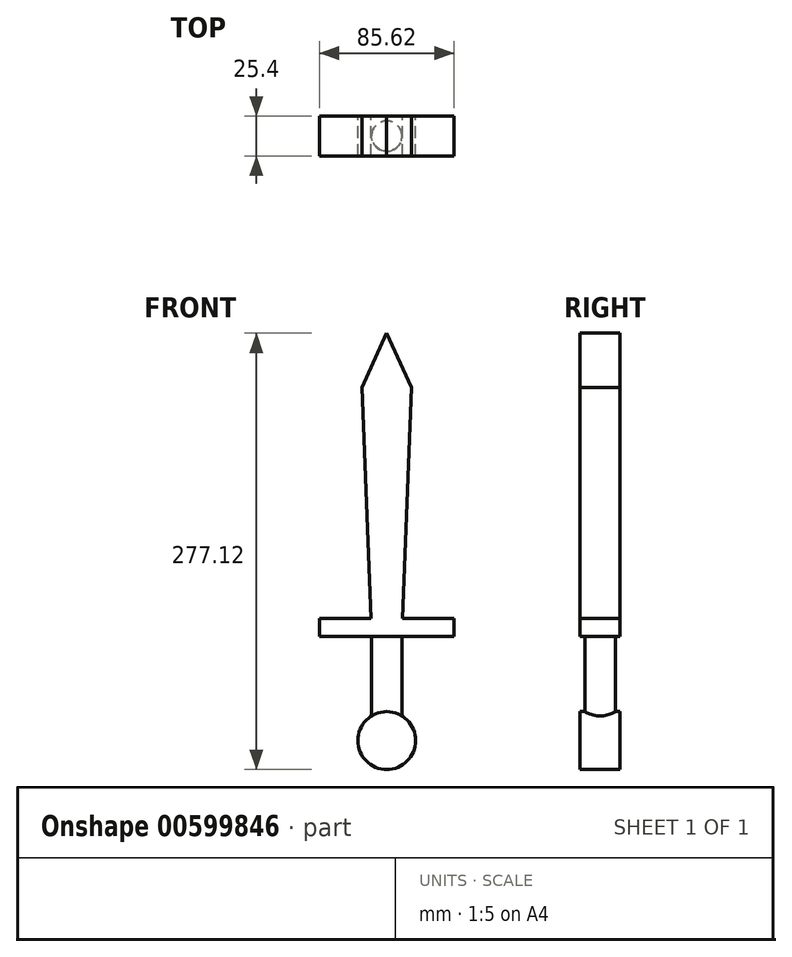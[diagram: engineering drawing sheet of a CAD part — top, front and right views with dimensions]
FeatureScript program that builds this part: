
annotation { "Feature Type Name" : "Feature", "Feature Type Description" : "" }
export const myFeature = defineFeature(function(context is Context, id is Id, definition is map)
    precondition{}
    {
        {
            var Q0;
            Q0=qCreatedBy(makeId("Front.planeOp"),FACE);
            var sketch = newSketch(context, id + "F0", { "sketchPlane" : qUnion([Q0])});
            skCircle(sketch, "E0", {"center": v(0, -49.9) * mm, "radius": 18.37 * mm});
            skLineSegment(sketch, "E1", {"start": v(0, -49.9) * mm, "end": v(0, 22) * mm});
            skLineSegment(sketch, "E2.bottom", {"start": v(0, 22) * mm, "end": v(9.7, 22) * mm});
            skLineSegment(sketch, "E2.top", {"start": v(0, -51.8) * mm, "end": v(9.7, -51.8) * mm});
            skLineSegment(sketch, "E2.left", {"start": v(0, 22) * mm, "end": v(0, -51.8) * mm});
            skLineSegment(sketch, "E2.right", {"start": v(9.7, 22) * mm, "end": v(9.7, -51.8) * mm});
            skLineSegment(sketch, "E3.bottom", {"start": v(0, -51.8) * mm, "end": v(-9.7, -51.8) * mm});
            skLineSegment(sketch, "E3.top", {"start": v(0, 22) * mm, "end": v(-9.7, 22) * mm});
            skLineSegment(sketch, "E3.left", {"start": v(0, -51.8) * mm, "end": v(0, 22) * mm});
            skLineSegment(sketch, "E3.right", {"start": v(-9.7, -51.8) * mm, "end": v(-9.7, 22) * mm});
            skLineSegment(sketch, "E4.bottom", {"start": v(42.81, 27.67) * mm, "end": v(-42.81, 27.67) * mm});
            skLineSegment(sketch, "E4.top", {"start": v(42.81, 16.32) * mm, "end": v(-42.81, 16.32) * mm});
            skLineSegment(sketch, "E4.left", {"start": v(42.81, 27.67) * mm, "end": v(42.81, 16.32) * mm});
            skLineSegment(sketch, "E4.right", {"start": v(-42.81, 27.67) * mm, "end": v(-42.81, 16.32) * mm});
            skPoint(sketch, "E4.middle", {"position": v(0, 22) * mm});
            skLineSegment(sketch, "E5", {"start": v(-9.7, 22) * mm, "end": v(-15.85, 174.32) * mm});
            skLineSegment(sketch, "E6", {"start": v(-15.85, 174.32) * mm, "end": v(0, 208.85) * mm});
            skLineSegment(sketch, "E7.MirrorCS", {"start": v(15.85, 174.32) * mm, "end": v(0, 208.85) * mm});
            skLineSegment(sketch, "E8.MirrorCS", {"start": v(9.7, 22) * mm, "end": v(15.85, 174.32) * mm});
            skSolve(sketch);
        }
        {
            var Q0;
            {var subQ6=sQuery(id+"F0.wireOp",EDGE,"E6");Q0=makeQuery(id+"F0.imprint","IMPRINT",FACE,{"disambiguationData":[TD([[makeQuery(id+"F0.imprint","IMPRINT",EDGE,{"derivedFrom":subQ6}),-1.0]])]});}
            var Q1;
            {var subQ0=sQuery(id+"F0.wireOp",EDGE,"E4.left");Q1=makeQuery(id+"F0.imprint","IMPRINT",FACE,{"disambiguationData":[TD([[makeQuery(id+"F0.imprint","IMPRINT",EDGE,{"derivedFrom":subQ0}),-1.0]])]});}
            var Q2;
            {var subQ0=sQuery(id+"F0.wireOp",EDGE,"E4.right");Q2=makeQuery(id+"F0.imprint","IMPRINT",FACE,{"disambiguationData":[TD([[makeQuery(id+"F0.imprint","IMPRINT",EDGE,{"derivedFrom":subQ0}),1.0]])]});}
            var Q3;
            {var subQ6=sQuery(id+"F0.wireOp",EDGE,"E2.bottom");Q3=makeQuery(id+"F0.imprint","IMPRINT",FACE,{"disambiguationData":[TD([[makeQuery(id+"F0.imprint","IMPRINT",EDGE,{"derivedFrom":subQ6}),1.0]])]});}
            var Q4;
            {var subQ0=sQuery(id+"F0.wireOp",EDGE,"E2.bottom");Q4=makeQuery(id+"F0.imprint","IMPRINT",FACE,{"disambiguationData":[TD([[makeQuery(id+"F0.imprint","IMPRINT",EDGE,{"derivedFrom":subQ0}),-1.0]])]});}
            var Q5;
            {var subQ0=sQuery(id+"F0.wireOp",EDGE,"E3.top");Q5=makeQuery(id+"F0.imprint","IMPRINT",FACE,{"disambiguationData":[TD([[makeQuery(id+"F0.imprint","IMPRINT",EDGE,{"derivedFrom":subQ0}),1.0]])]});}
            extrude(context, id + "F1", {"entities" : qUnion([Q0, Q1, Q2, Q3, Q4, Q5]), "endBound" : BoundingType.SYMMETRIC, "depth" : 25.4 * mm, "offsetDistance" : 25.4 * mm});
        }
        {
            var Q0;
            {var subQ0=sQuery(id+"F0.wireOp",EDGE,"E2.right");var subQ1=sQuery(id+"F0.wireOp",EDGE,"E0");var subQ2=makeQuery(id+"F0.imprint","INTERSECT",VERTEX,{"derivedFrom":[subQ1,subQ0]});Q0=makeQuery(id+"F0.imprint","IMPRINT",FACE,{"disambiguationData":[TD([[makeQuery(id+"F0.imprint","IMPRINT",EDGE,{"disambiguationData":[TD([[subQ2,-1.0]])],"derivedFrom":subQ1}),-1.0]])]});}
            var Q1;
            Q1=sQuery(id+"F0.wireOp",EDGE,"E3.left");
            revolve(context, id + "F2", {"entities" : qUnion([Q0]), "axis" : qUnion([Q1]), "revolveType" : RevolveType.SYMMETRIC, "angle" : 360 * degree});
        }
        {
            var Q0;
            {var subQ1=sQuery(id+"F0.wireOp",EDGE,"E2.top");Q0=makeQuery(id+"F0.imprint","IMPRINT",FACE,{"disambiguationData":[TD([[makeQuery(id+"F0.imprint","IMPRINT",EDGE,{"derivedFrom":subQ1}),-1.0]])]});}
            var Q1;
            {var subQ1=sQuery(id+"F0.wireOp",EDGE,"E3.bottom");Q1=makeQuery(id+"F0.imprint","IMPRINT",FACE,{"disambiguationData":[TD([[makeQuery(id+"F0.imprint","IMPRINT",EDGE,{"derivedFrom":subQ1}),-1.0]])]});}
            var Q2;
            {var subQ1=sQuery(id+"F0.wireOp",EDGE,"E2.top");Q2=makeQuery(id+"F0.imprint","IMPRINT",FACE,{"disambiguationData":[TD([[makeQuery(id+"F0.imprint","IMPRINT",EDGE,{"derivedFrom":subQ1}),1.0]])]});}
            extrude(context, id + "F3", {"entities" : qUnion([Q0, Q1, Q2]), "operationType" : NewBodyOperationType.ADD, "endBound" : BoundingType.SYMMETRIC, "depth" : 25.4 * mm, "offsetDistance" : 25.4 * mm});
        }
    });
